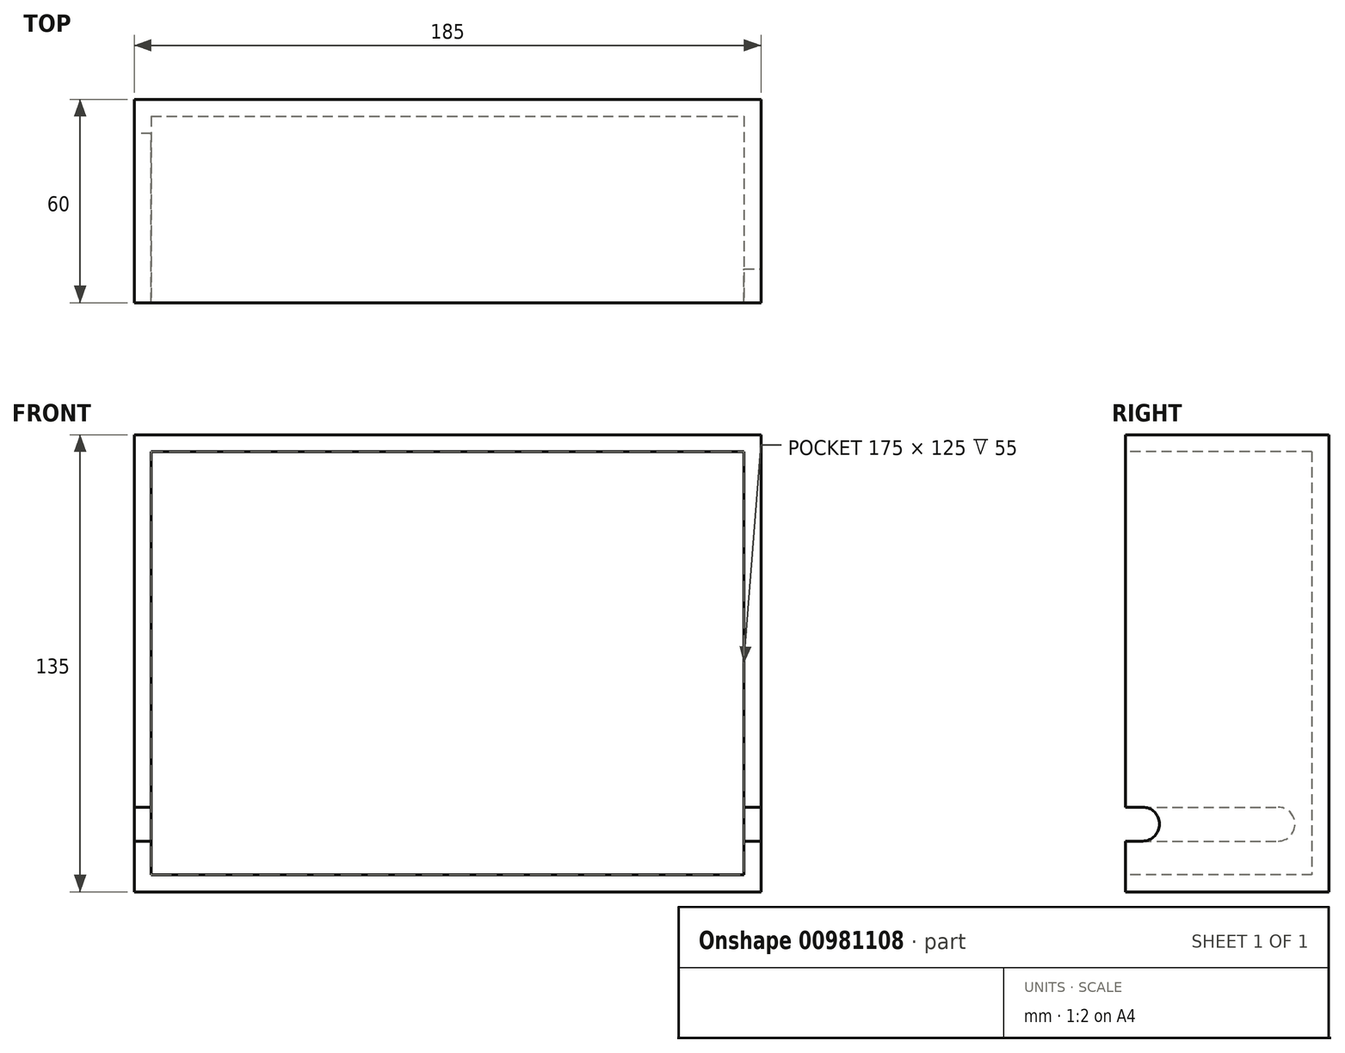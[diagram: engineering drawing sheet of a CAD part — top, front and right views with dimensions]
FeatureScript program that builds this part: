
annotation { "Feature Type Name" : "Feature", "Feature Type Description" : "" }
export const myFeature = defineFeature(function(context is Context, id is Id, definition is map)
    precondition{}
    {
        {
            var Q0;
            Q0=qCreatedBy(makeId("Front.planeOp"),FACE);
            var sketch = newSketch(context, id + "F0", { "sketchPlane" : qUnion([Q0])});
            skLineSegment(sketch, "E0.bottom", {"start": v(0, 0) * mm, "end": v(185, 0) * mm});
            skLineSegment(sketch, "E0.top", {"start": v(0, 135) * mm, "end": v(185, 135) * mm});
            skLineSegment(sketch, "E0.left", {"start": v(0, 0) * mm, "end": v(0, 135) * mm});
            skLineSegment(sketch, "E0.right", {"start": v(185, 0) * mm, "end": v(185, 135) * mm});
            skSolve(sketch);
        }
        {
            var Q0;
            Q0 = qSketchRegion(id + "F0", true);
            extrude(context, id + "F1", {"entities" : qUnion([Q0]), "depth" : 60 * mm, "offsetDistance" : 25 * mm});
        }
        {
            var Q0;
            Q0=makeQuery(id+"F1.opExtrude","CAP_FACE",FACE,{"disambiguationData":[OSD([sQuery(id+"F0.wireOp",EDGE,"E0.bottom"),sQuery(id+"F0.wireOp",EDGE,"E0.top"),sQuery(id+"F0.wireOp",EDGE,"E0.left"),sQuery(id+"F0.wireOp",EDGE,"E0.right")])],"isStart":false});
            var sketch = newSketch(context, id + "F2", { "sketchPlane" : qUnion([Q0])});
            skLineSegment(sketch, "E1.bottom", {"start": v(5, 130) * mm, "end": v(180, 130) * mm});
            skLineSegment(sketch, "E1.top", {"start": v(5, 5) * mm, "end": v(180, 5) * mm});
            skLineSegment(sketch, "E1.left", {"start": v(5, 130) * mm, "end": v(5, 5) * mm});
            skLineSegment(sketch, "E1.right", {"start": v(180, 130) * mm, "end": v(180, 5) * mm});
            skSolve(sketch);
        }
        {
            var Q0;
            Q0 = qSketchRegion(id + "F2", true);
            extrude(context, id + "F3", {"entities" : qUnion([Q0]), "operationType" : NewBodyOperationType.REMOVE, "oppositeDirection" : true, "depth" : 55 * mm, "offsetDistance" : 25 * mm});
        }
        {
            var Q0;
            Q0=makeQuery(id+"F1.opExtrude","SWEPT_FACE",FACE,{"disambiguationData":[OSD([sQuery(id+"F0.wireOp",EDGE,"E0.right")])]});
            var sketch = newSketch(context, id + "F4", { "sketchPlane" : qUnion([Q0])});
            skCircle(sketch, "E2", {"center": v(-55, 20) * mm, "radius": 5 * mm});
            skLineSegment(sketch, "E3.bottom", {"start": v(-55, 25) * mm, "end": v(-65, 25) * mm});
            skLineSegment(sketch, "E3.top", {"start": v(-55, 15) * mm, "end": v(-65, 15) * mm});
            skLineSegment(sketch, "E3.left", {"start": v(-55, 25) * mm, "end": v(-55, 15) * mm});
            skLineSegment(sketch, "E3.right", {"start": v(-65, 25) * mm, "end": v(-65, 15) * mm});
            skPoint(sketch, "E3.middle", {"position": v(-60, 20) * mm});
            skSolve(sketch);
        }
        {
            var Q0;
            Q0 = qSketchRegion(id + "F4", true);
            extrude(context, id + "F5", {"entities" : qUnion([Q0]), "operationType" : NewBodyOperationType.REMOVE, "oppositeDirection" : true, "depth" : 25 * mm, "offsetDistance" : 25 * mm});
        }
        {
            var Q0;
            Q0=makeQuery(id+"F1.opExtrude","SWEPT_FACE",FACE,{"disambiguationData":[OSD([sQuery(id+"F0.wireOp",EDGE,"E0.left")])]});
            var sketch = newSketch(context, id + "F6", { "sketchPlane" : qUnion([Q0])});
            skLineSegment(sketch, "E4.bottom", {"start": v(60, 25) * mm, "end": v(15, 25) * mm});
            skLineSegment(sketch, "E4.top", {"start": v(60, 15) * mm, "end": v(15, 15) * mm});
            skLineSegment(sketch, "E4.left", {"start": v(60, 25) * mm, "end": v(60, 15) * mm});
            skLineSegment(sketch, "E4.right", {"start": v(15, 25) * mm, "end": v(15, 15) * mm});
            skCircle(sketch, "E5", {"center": v(15, 20) * mm, "radius": 5 * mm});
            skSolve(sketch);
        }
        {
            var Q0;
            Q0 = qSketchRegion(id + "F6", true);
            extrude(context, id + "F7", {"entities" : qUnion([Q0]), "operationType" : NewBodyOperationType.REMOVE, "oppositeDirection" : true, "depth" : 25 * mm, "offsetDistance" : 25 * mm});
        }
    });
